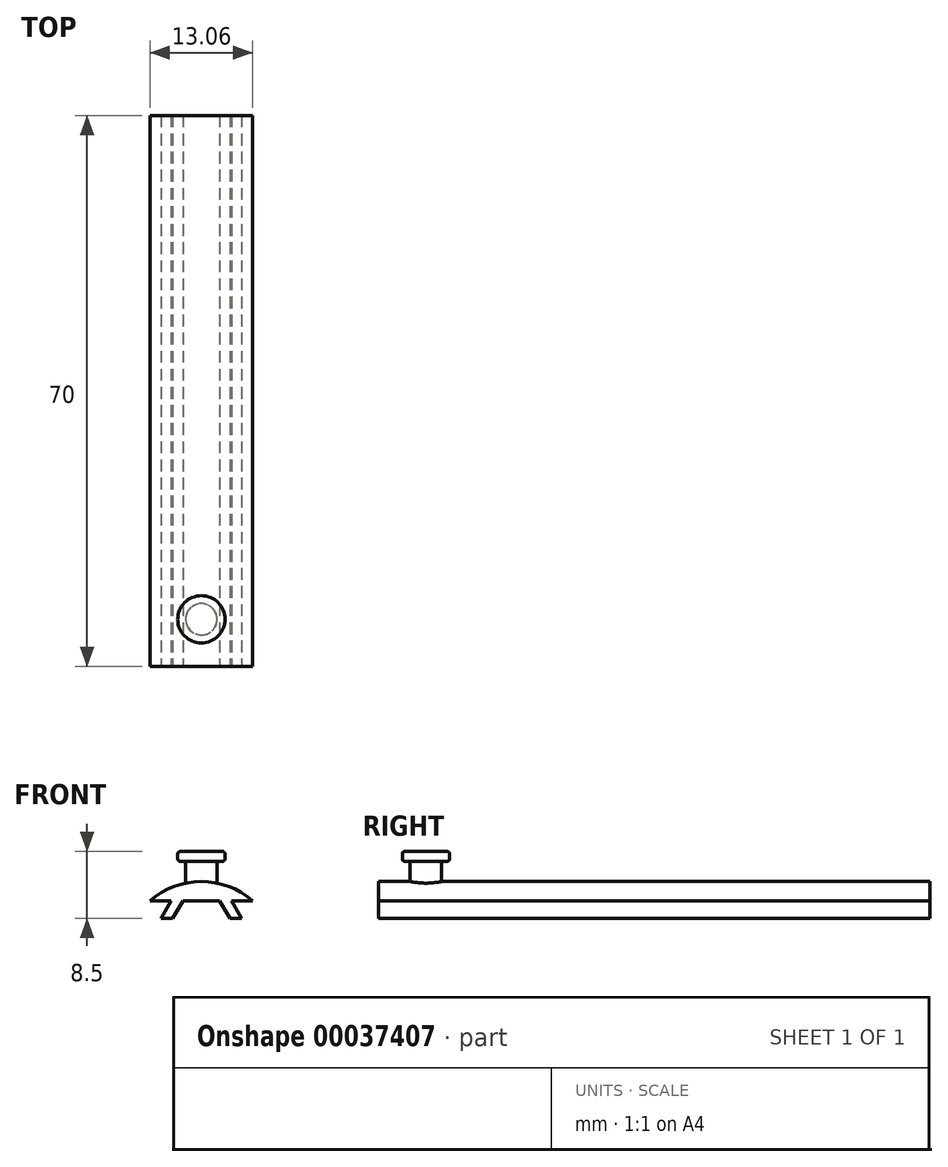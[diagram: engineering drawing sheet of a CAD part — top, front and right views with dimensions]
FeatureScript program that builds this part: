
annotation { "Feature Type Name" : "Feature", "Feature Type Description" : "" }
export const myFeature = defineFeature(function(context is Context, id is Id, definition is map)
    precondition{}
    {
        {
            var Q0;
            Q0=qCreatedBy(makeId("Front.planeOp"),FACE);
            var sketch = newSketch(context, id + "F0", { "sketchPlane" : qUnion([Q0])});
            skArc(sketch, "E0", {"start": v(6.53, 7.57) * mm, "mid": v(0, 10) * mm, "end": v(-6.53, 7.57) * mm});
            skLineSegment(sketch, "E1", {"start": v(-5.13, 5.32) * mm, "end": v(-3.83, 7.57) * mm});
            skLineSegment(sketch, "E2", {"start": v(-3.83, 7.57) * mm, "end": v(-6.53, 7.57) * mm});
            skLineSegment(sketch, "E3", {"start": v(-5.13, 5.32) * mm, "end": v(-3.63, 5.32) * mm});
            skLineSegment(sketch, "E4", {"start": v(-3.63, 5.32) * mm, "end": v(-2.33, 7.57) * mm});
            skLineSegment(sketch, "E5", {"start": v(-2.33, 7.57) * mm, "end": v(0, 7.57) * mm});
            skLineSegment(sketch, "E6.MirrorCS", {"start": v(2.33, 7.57) * mm, "end": v(0, 7.57) * mm});
            skLineSegment(sketch, "E7.MirrorCS", {"start": v(3.63, 5.32) * mm, "end": v(2.33, 7.57) * mm});
            skLineSegment(sketch, "E8.MirrorCS", {"start": v(5.13, 5.32) * mm, "end": v(3.83, 7.57) * mm});
            skLineSegment(sketch, "E9.MirrorCS", {"start": v(3.83, 7.57) * mm, "end": v(6.53, 7.57) * mm});
            skLineSegment(sketch, "E10.MirrorCS", {"start": v(5.13, 5.32) * mm, "end": v(3.63, 5.32) * mm});
            skSolve(sketch);
        }
        {
            var Q0;
            Q0 = qSketchRegion(id + "F0", true);
            extrude(context, id + "F1", {"entities" : qUnion([Q0]), "oppositeDirection" : true, "depth" : 70 * mm});
        }
        {
            var Q0;
            Q0=makeQuery(id+"F1.opExtrude","SWEPT_FACE",FACE,{"disambiguationData":[OSD([sQuery(id+"F0.wireOp",EDGE,"E5"),sQuery(id+"F0.wireOp",EDGE,"E6.MirrorCS")])]});
            var sketch = newSketch(context, id + "F2", { "sketchPlane" : qUnion([Q0])});
            skCircle(sketch, "E11", {"center": v(0, -6) * mm, "radius": 2 * mm});
            skSolve(sketch);
        }
        {
            var Q0;
            Q0 = qSketchRegion(id + "F2", true);
            extrude(context, id + "F3", {"entities" : qUnion([Q0]), "operationType" : NewBodyOperationType.ADD, "oppositeDirection" : true, "depth" : 5 * mm});
        }
        {
            var Q0;
            Q0=makeQuery(id+"F3.opExtrude","CAP_FACE",FACE,{"disambiguationData":[OSD([sQuery(id+"F2.wireOp",EDGE,"E11")])],"isStart":false});
            var sketch = newSketch(context, id + "F4", { "sketchPlane" : qUnion([Q0])});
            skCircle(sketch, "E12", {"center": v(0, 6) * mm, "radius": 3 * mm});
            skSolve(sketch);
        }
        {
            var Q0;
            Q0 = qSketchRegion(id + "F4", true);
            extrude(context, id + "F5", {"entities" : qUnion([Q0]), "operationType" : NewBodyOperationType.ADD, "depth" : 1.25 * mm});
        }
        {
            var Q0;
            Q0=makeQuery(id+"F5.opExtrude","CAP_EDGE",EDGE,{"disambiguationData":[OSD([sQuery(id+"F4.wireOp",EDGE,"E12")])],"isStart":false});
            var Q1;
            Q1=makeQuery(id+"F5.opExtrude","CAP_EDGE",EDGE,{"disambiguationData":[OSD([sQuery(id+"F4.wireOp",EDGE,"E12")])],"isStart":true});
            fillet(context, id + "F6", {"entities" : qUnion([Q0, Q1]), "radius" : 0.3 * mm, "tangentPropagation" : true, "allowEdgeOverflow" : false});
        }
    });
